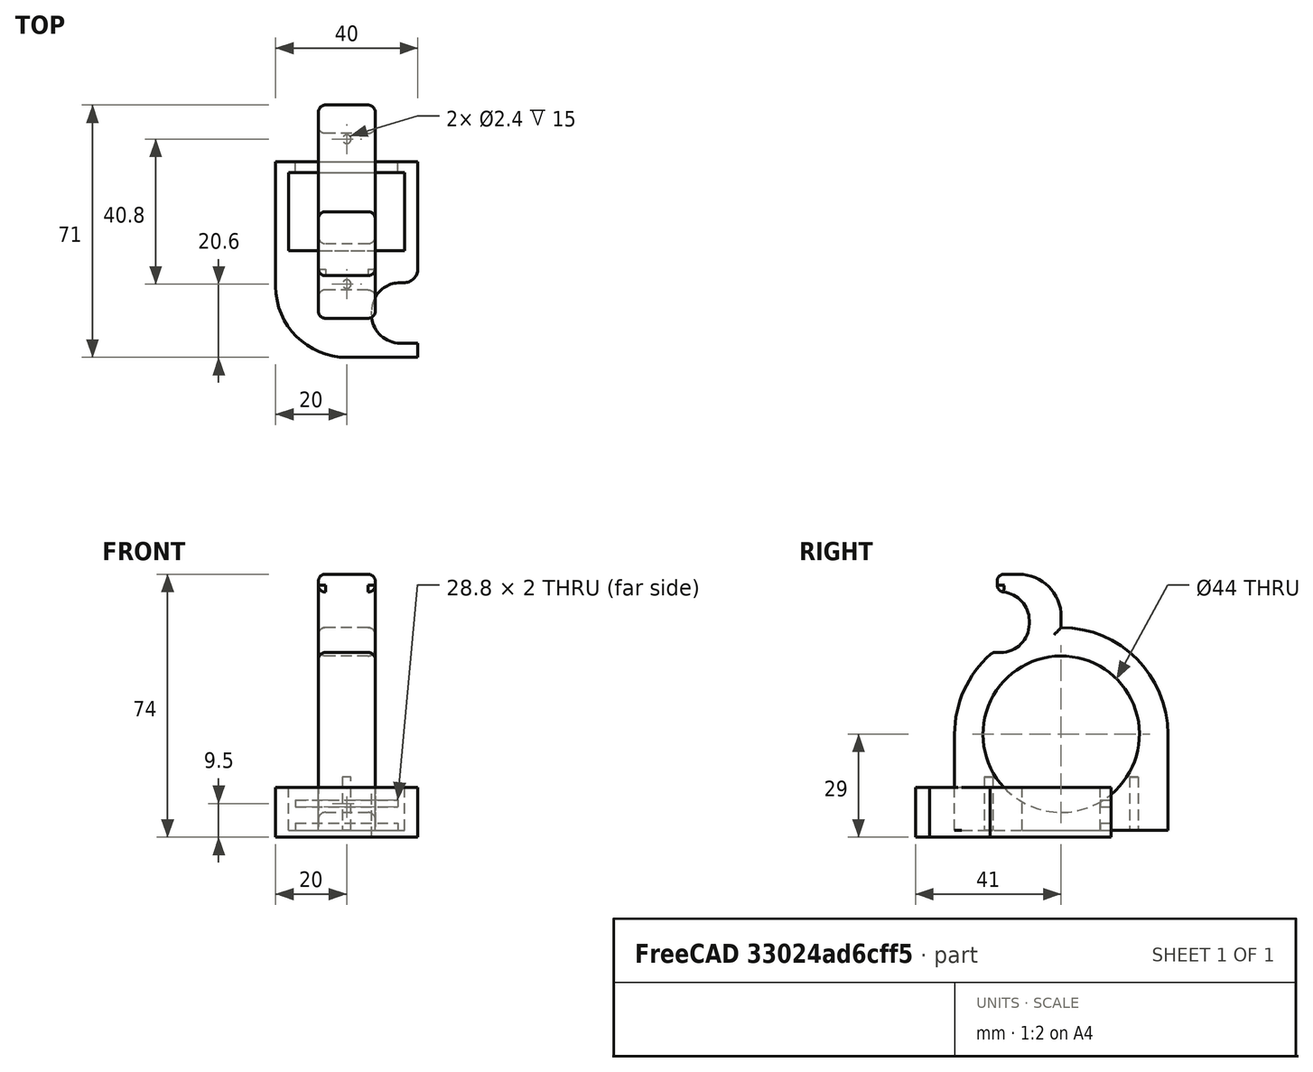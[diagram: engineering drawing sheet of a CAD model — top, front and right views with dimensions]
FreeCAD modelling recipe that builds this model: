
FCSTD DOCUMENT  (FreeCAD 0.20R29177 +426 (Git))
Label: Garnisna
License: All rights reserved
LicenseURL: http://en.wikipedia.org/wiki/All_rights_reserved
objects: Part::Box×10, Part::Fillet×8, Part::Cylinder×5, Part::Cut×4, Part::MultiFuse×3
note: 30 computed .brp shape members not serialized (recipe doc carries the construction recipe); baked Part::Feature solids carry a one-line shape summary decoded from their .brp

FEATURE [Part::Box] Box004  label="Cube004"
  AttacherType = Attacher::AttachEngine3D
  Height = 12
  Length = 32.6
  Placement = pos=(-16.3,-11,0) rot=(0,0,1;0rad)
  Width = 22
FEATURE [Part::Box] Box005  label="Cube005"
  AttacherType = Attacher::AttachEngine3D
  Height = 2
  Length = 28.8
  Placement = pos=(-14.4,0,0) rot=(0,0,1;0rad)
  Width = 22
FEATURE [Part::Box] Box006  label="Cube006"
  AttacherType = Attacher::AttachEngine3D
  Height = 2
  Length = 28.8
  Placement = pos=(-14.4,0,6.5) rot=(0,0,1;0rad)
  Width = 22
FEATURE [Part::MultiFuse] Fusion  label="Hollows"
  Shapes = -> [Box004,Box005,Box006]
FEATURE [Part::Box] Box007  label="Cube007"
  AttacherType = Attacher::AttachEngine3D
  Height = 14
  Length = 40
  Placement = pos=(-20,-41,-2) rot=(0,0,1;0rad)
  Width = 55
FEATURE [Part::Box] Box  label="Cube"
  AttacherType = Attacher::AttachEngine3D
  Height = 20
  Length = 20
  Placement = pos=(7,-37,-3) rot=(0,0,1;0rad)
  Width = 17
FEATURE [Part::Fillet] Fillet
  Base = -> Box
  Edges = 2 edges r=8: [Edge1,Edge3]
FEATURE [Part::MultiFuse] Fusion001
  Shapes = -> [Fillet,Fusion]
FEATURE [Part::Fillet] Fillet001
  Base = -> Box007
  Edges = 1 edges r=20: [Edge1]
FEATURE [Part::Cut] Cut
  Base = -> Fillet001
  Tool = -> Fusion001
FEATURE [Part::Fillet] Fillet002  label="StaraKuka"
  Base = -> Cut
  Edges = 1 edges r=4: [Edge39]
FEATURE [Part::Box] Box010  label="Body"
  AttacherType = Attacher::AttachEngine3D
  Height = 72
  Length = 16
  Placement = pos=(-8,-30,0) rot=(0,0,1;0rad)
  Width = 60
FEATURE [Part::Box] Box011  label="Cube008"
  AttacherType = Attacher::AttachEngine3D
  Height = 17
  Length = 20
  Placement = pos=(-10,-30,50) rot=(0,0,1;0rad)
  Width = 21
FEATURE [Part::Fillet] Fillet004
  Base = -> Box011
  Edges = 2 edges r=8: [Edge11,Edge12]
FEATURE [Part::Box] Box012  label="Cube009"
  AttacherType = Attacher::AttachEngine3D
  Height = 10
  Length = 20
  Placement = pos=(-10,-30,63) rot=(0,0,1;0rad)
  Width = 12
FEATURE [Part::Cylinder] Cylinder  label="Screw001"
  Angle = 360
  AttacherType = Attacher::AttachEngine3D
  FirstAngle = 0
  Height = 15
  Placement = pos=(0,20.4,0) rot=(0,0,1;0rad)
  Radius = 1.2
  SecondAngle = 0
FEATURE [Part::Cylinder] Cylinder001  label="Screw002"
  Angle = 360
  AttacherType = Attacher::AttachEngine3D
  FirstAngle = 0
  Height = 15
  Placement = pos=(0,-20.4,0) rot=(0,0,1;0rad)
  Radius = 1.2
  SecondAngle = 0
FEATURE [Part::Cylinder] Cylinder002  label="Cylinder"
  Angle = 360
  AttacherType = Attacher::AttachEngine3D
  FirstAngle = 0
  Height = 20
  Placement = pos=(-10,0,27) rot=(0,1,0;1.5708rad)
  Radius = 22
  SecondAngle = 0
FEATURE [Part::Box] Box013  label="Body001"
  AttacherType = Attacher::AttachEngine3D
  Height = 30
  Length = 20
  Placement = pos=(-10,-35,27) rot=(0,0,1;0rad)
  Width = 20
FEATURE [Part::Cylinder] Cylinder003
  Angle = 360
  AttacherType = Attacher::AttachEngine3D
  FirstAngle = 0
  Height = 20
  Placement = pos=(-10,0,27) rot=(0,1,0;1.5708rad)
  Radius = 30
  SecondAngle = 0
FEATURE [Part::Cut] Cut001  label="Limit_001"
  Base = -> Box013
  Tool = -> Cylinder003
FEATURE [Part::Cylinder] Cylinder004
  Angle = 360
  AttacherType = Attacher::AttachEngine3D
  FirstAngle = 0
  Height = 20
  Placement = pos=(-10,0,27) rot=(0,1,0;1.5708rad)
  Radius = 30
  SecondAngle = 0
FEATURE [Part::Box] Box014  label="Body002"
  AttacherType = Attacher::AttachEngine3D
  Height = 50
  Length = 20
  Placement = pos=(-10,0,27) rot=(0,0,1;0rad)
  Width = 30
FEATURE [Part::Cut] Cut002  label="Limit_002"
  Base = -> Box014
  Tool = -> Cylinder004
FEATURE [Part::MultiFuse] Fusion002  label="Hollows001"
  Shapes = -> [Cut001,Cut002,Cylinder002,Cylinder001,Cylinder,Box012,Fillet004]
FEATURE [Part::Cut] Cut003
  Base = -> Box010
  Tool = -> Fusion002
FEATURE [Part::Fillet] Fillet005
  Base = -> Cut003
  Edges = 1 edges r=12: [Edge32]
FEATURE [Part::Fillet] Fillet006
  Base = -> Fillet005
  Edges = 3 edges r=2: [Edge16,Edge22,Edge44]
FEATURE [Part::Fillet] Fillet007
  Base = -> Fillet006
  Edges = 4 edges r=2: [Edge10,Edge14,Edge31,Edge50]
FEATURE [Part::Fillet] Fillet008  label="Drzac"
  Base = -> Fillet007
  Edges = 2 edges r=2: [Edge14,Edge51]
